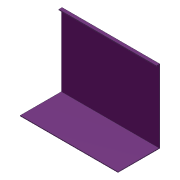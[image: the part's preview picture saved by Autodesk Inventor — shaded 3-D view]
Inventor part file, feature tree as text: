
AUTODESK INVENTOR PART (.ipt)
format: ipt  version: 2012 (Build 160160000, 160)  size: 154,112 bytes
history: native  units: in
note: dims shown in document units (in); Inventor stores cm internally (conversion verified against a paired STEP export)
features: extrude x6, sketch x6
ambient origin geometry x8: Origin, YZ Plane, XZ Plane, XY Plane, X Axis, Y Axis, Z Axis, Center Point
bodies: Solid1 (feature_tree)
feature tree (12):
  extrude  "Extrusion1"  Depth=0.0625in
  extrude  "Extrusion2"  Depth=4.0in
  extrude  "Extrusion3"  Depth=9.5in TaperAngle=0.0deg
  extrude  "Extrusion4"  Depth=2.0in
  extrude  "Extrusion5"  Depth=9.5in TaperAngle=0.0deg
  extrude  "Extrusion6"  Depth=1.0in TaperAngle=0.0deg
  sketch  "Sketch1"  dims[d0=0.0625in d1=0.0625in]
  sketch  "Sketch2"  dims[d2=7.125in d3=4.0in]
  sketch  "Sketch3"  dims[d4=0.25in d5=9.5in d6=0.0in]
  sketch  "Sketch4"  dims[d7=1.0in d8=2.0in]
  sketch  "Sketch5"  dims[d9=3.0in d10=9.5in d11=0.0in]
  sketch  "Sketch6"  dims[d12=0.0625in d13=1.0in d14=0.0in d15=0.251in d16=0.5in d18=1.0in d19=4.0in d20=0.5in d21=1.0in d22=0.0in d23=1.25in d24=1.0in d25=0.0in d26=0.5in d27=0.5in d28=3.5in d29=0.25in d30=1.0in d31=0.0in]
